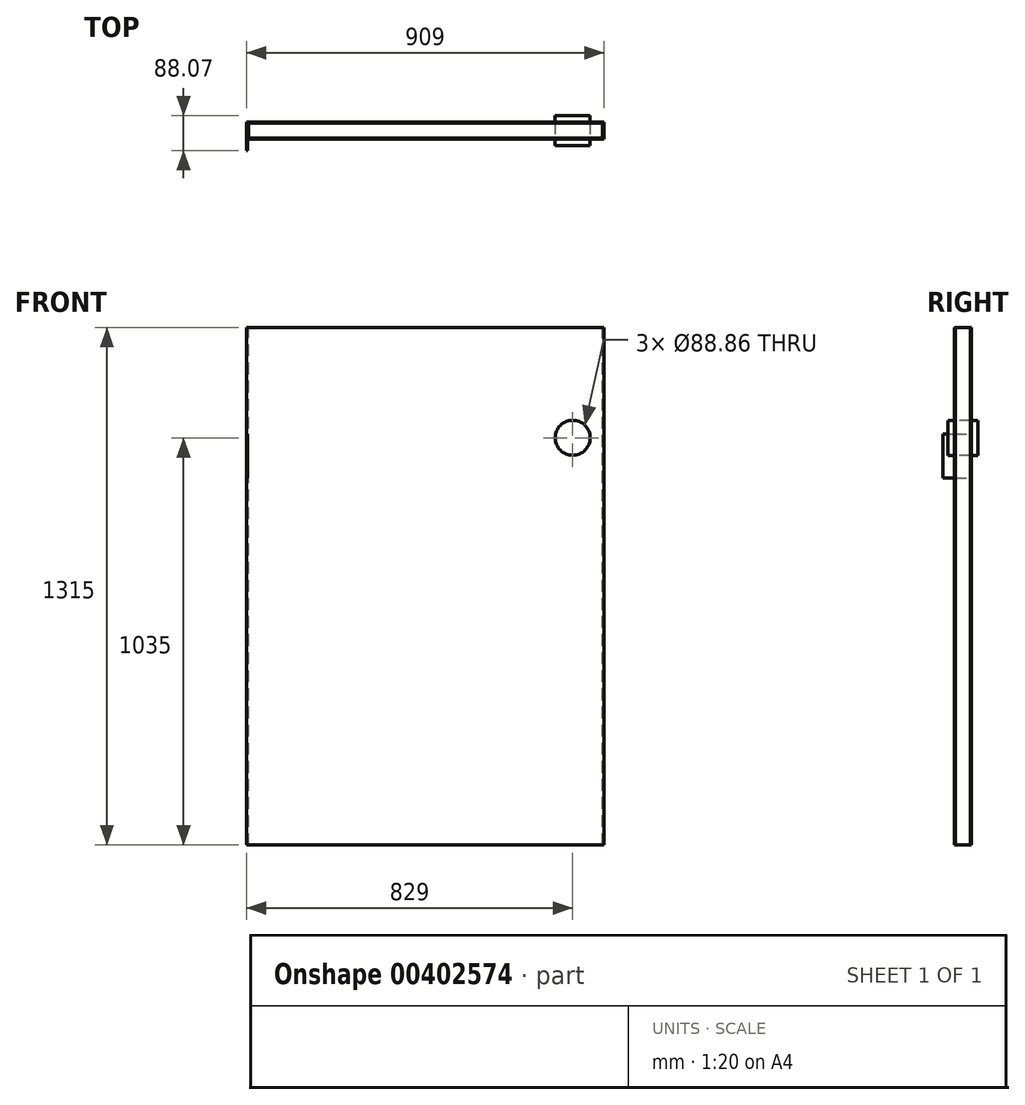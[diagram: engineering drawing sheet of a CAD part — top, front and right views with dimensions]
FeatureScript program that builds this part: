
annotation { "Feature Type Name" : "Feature", "Feature Type Description" : "" }
export const myFeature = defineFeature(function(context is Context, id is Id, definition is map)
    precondition{}
    {
        {
            var Q0;
            Q0=qCreatedBy(makeId("Front.planeOp"),FACE);
            var sketch = newSketch(context, id + "F0", { "sketchPlane" : qUnion([Q0])});
            skLineSegment(sketch, "E0.bottom", {"start": v(-454.5, 657.5) * mm, "end": v(454.5, 657.5) * mm});
            skLineSegment(sketch, "E0.top", {"start": v(-454.5, -657.5) * mm, "end": v(454.5, -657.5) * mm});
            skLineSegment(sketch, "E0.left", {"start": v(-454.5, 657.5) * mm, "end": v(-454.5, -657.5) * mm});
            skLineSegment(sketch, "E0.right", {"start": v(454.5, 657.5) * mm, "end": v(454.5, -657.5) * mm});
            skPoint(sketch, "E0.middle", {"position": v(0, 0) * mm});
            skSolve(sketch);
        }
        {
            var Q0;
            Q0=makeQuery(id+"F0.imprint","IMPRINT",FACE,{"disambiguationData":[TD([[makeQuery(id+"F0.imprint","IMPRINT",EDGE,{"derivedFrom":sQuery(id+"F0.wireOp",EDGE,"E0.bottom")}),-1.0]])]});
            extrude(context, id + "F1", {"entities" : qUnion([Q0]), "depth" : 43.25 * mm});
        }
        {
            var Q0;
            Q0=makeQuery(id+"F1.opExtrude","CAP_FACE",FACE,{"disambiguationData":[OSD([sQuery(id+"F0.wireOp",EDGE,"E0.bottom"),sQuery(id+"F0.wireOp",EDGE,"E0.top"),sQuery(id+"F0.wireOp",EDGE,"E0.left"),sQuery(id+"F0.wireOp",EDGE,"E0.right")])],"isStart":false});
            extrude(context, id + "F2", {"entities" : qUnion([Q0]), "oppositeDirection" : true, "depth" : 2.81 * mm});
        }
        {
            var Q0;
            Q0=makeQuery(id+"F1.opExtrude","CAP_FACE",FACE,{"disambiguationData":[OSD([sQuery(id+"F0.wireOp",EDGE,"E0.bottom"),sQuery(id+"F0.wireOp",EDGE,"E0.top"),sQuery(id+"F0.wireOp",EDGE,"E0.left"),sQuery(id+"F0.wireOp",EDGE,"E0.right")])],"isStart":true});
            extrude(context, id + "F3", {"entities" : qUnion([Q0]), "oppositeDirection" : true, "depth" : 2.81 * mm});
        }
        {
            var Q0;
            Q0=makeQuery(id+"F1.opExtrude","CAP_FACE",FACE,{"disambiguationData":[OSD([sQuery(id+"F0.wireOp",EDGE,"E0.bottom"),sQuery(id+"F0.wireOp",EDGE,"E0.top"),sQuery(id+"F0.wireOp",EDGE,"E0.left"),sQuery(id+"F0.wireOp",EDGE,"E0.right")])],"isStart":false});
            var sketch = newSketch(context, id + "F4", { "sketchPlane" : qUnion([Q0])});
            skLineSegment(sketch, "E1", {"start": v(407.48, 657.5) * mm, "end": v(407.48, 377.5) * mm});
            skLineSegment(sketch, "E2", {"start": v(454.5, 377.5) * mm, "end": v(374.5, 377.5) * mm});
            skPoint(sketch, "E3", {"position": v(374.5, 377.5) * mm});
            skCircle(sketch, "E4", {"center": v(374.5, 377.5) * mm, "radius": 44.43 * mm});
            skSolve(sketch);
        }
        {
            var Q0;
            {var subQ0=sQuery(id+"F4.wireOp",EDGE,"E2");var subQ1=sQuery(id+"F4.wireOp",EDGE,"E1");var subQ2=makeQuery(id+"F4.imprint","INTERSECT",VERTEX,{"derivedFrom":[subQ1,subQ0]});Q0=makeQuery(id+"F4.imprint","IMPRINT",FACE,{"disambiguationData":[TD([[makeQuery(id+"F4.imprint","IMPRINT",EDGE,{"disambiguationData":[TD([[subQ2,1.0]])],"derivedFrom":subQ1}),1.0]])]});}
            var Q1;
            {var subQ0=sQuery(id+"F4.wireOp",EDGE,"E2");var subQ1=sQuery(id+"F4.wireOp",EDGE,"E1");var subQ2=makeQuery(id+"F4.imprint","INTERSECT",VERTEX,{"derivedFrom":[subQ1,subQ0]});Q1=makeQuery(id+"F4.imprint","IMPRINT",FACE,{"disambiguationData":[TD([[makeQuery(id+"F4.imprint","IMPRINT",EDGE,{"disambiguationData":[TD([[subQ2,1.0]])],"derivedFrom":subQ1}),-1.0]])]});}
            extrude(context, id + "F5", {"entities" : qUnion([Q0, Q1]), "operationType" : NewBodyOperationType.REMOVE, "endBound" : BoundingType.THROUGH_ALL, "oppositeDirection" : true, "depth" : 15.73 * mm});
        }
        {
            var Q0;
            Q0=makeQuery(id+"F1.opExtrude","CAP_FACE",FACE,{"disambiguationData":[OSD([sQuery(id+"F0.wireOp",EDGE,"E0.bottom"),sQuery(id+"F0.wireOp",EDGE,"E0.top"),sQuery(id+"F0.wireOp",EDGE,"E0.left"),sQuery(id+"F0.wireOp",EDGE,"E0.right")])],"isStart":true});
            var sketch = newSketch(context, id + "F6", { "sketchPlane" : qUnion([Q0])});
            skPoint(sketch, "E5", {"position": v(451.14, 387.5) * mm});
            skLineSegment(sketch, "E6.bottom", {"start": v(451.14, 387.5) * mm, "end": v(454.5, 387.5) * mm});
            skLineSegment(sketch, "E6.top", {"start": v(451.14, 274.8) * mm, "end": v(454.5, 274.8) * mm});
            skLineSegment(sketch, "E6.left", {"start": v(451.14, 387.5) * mm, "end": v(451.14, 274.8) * mm});
            skLineSegment(sketch, "E6.right", {"start": v(454.5, 387.5) * mm, "end": v(454.5, 274.8) * mm});
            skSolve(sketch);
        }
        {
            var Q0;
            Q0=makeQuery(id+"F6.imprint","IMPRINT",FACE,{"disambiguationData":[TD([[makeQuery(id+"F6.imprint","IMPRINT",EDGE,{"derivedFrom":sQuery(id+"F6.wireOp",EDGE,"E6.bottom")}),-1.0]])]});
            extrude(context, id + "F7", {"entities" : qUnion([Q0]), "operationType" : NewBodyOperationType.REMOVE, "endBound" : BoundingType.THROUGH_ALL, "oppositeDirection" : true, "depth" : 28 * mm});
        }
        {
            var Q0;
            Q0=makeQuery(id+"F1.opExtrude","CAP_FACE",FACE,{"disambiguationData":[OSD([sQuery(id+"F0.wireOp",EDGE,"E0.bottom"),sQuery(id+"F0.wireOp",EDGE,"E0.top"),sQuery(id+"F0.wireOp",EDGE,"E0.left"),sQuery(id+"F0.wireOp",EDGE,"E0.right")])],"isStart":false});
            var sketch = newSketch(context, id + "F8", { "sketchPlane" : qUnion([Q0])});
            skCircle(sketch, "E7.0", {"center": v(374.5, 377.5) * mm, "radius": 44.43 * mm});
            skSolve(sketch);
        }
        {
            var Q0;
            Q0=qSketchRegion(id+"F8",true);
            extrude(context, id + "F9", {"entities" : qUnion([Q0]), "depth" : 16 * mm});
        }
        {
            var Q0;
            Q0=makeQuery(id+"F3.opExtrude","CAP_FACE",FACE,{"disambiguationData":[OSD([sQuery(id+"F0.wireOp",EDGE,"E0.bottom"),sQuery(id+"F0.wireOp",EDGE,"E0.top"),sQuery(id+"F0.wireOp",EDGE,"E0.left"),sQuery(id+"F0.wireOp",EDGE,"E0.right")])],"isStart":true});
            var sketch = newSketch(context, id + "F10", { "sketchPlane" : qUnion([Q0])});
            skCircle(sketch, "E8.0", {"center": v(-374.5, 377.5) * mm, "radius": 44.43 * mm});
            skSolve(sketch);
        }
        {
            var Q0;
            Q0=qSketchRegion(id+"F10",true);
            extrude(context, id + "F11", {"entities" : qUnion([Q0]), "depth" : 16 * mm});
        }
        {
            var Q0;
            Q0=makeQuery(id+"F1.opExtrude","CAP_FACE",FACE,{"disambiguationData":[OSD([sQuery(id+"F0.wireOp",EDGE,"E0.bottom"),sQuery(id+"F0.wireOp",EDGE,"E0.top"),sQuery(id+"F0.wireOp",EDGE,"E0.left"),sQuery(id+"F0.wireOp",EDGE,"E0.right")])],"isStart":false});
            var sketch = newSketch(context, id + "F12", { "sketchPlane" : qUnion([Q0])});
            skLineSegment(sketch, "E9", {"start": v(-454.5, 387.5) * mm, "end": v(-454.5, 274.8) * mm});
            skLineSegment(sketch, "E10", {"start": v(-454.5, 274.8) * mm, "end": v(-451.14, 274.8) * mm});
            skLineSegment(sketch, "E11", {"start": v(-451.14, 274.8) * mm, "end": v(-451.14, 387.5) * mm});
            skLineSegment(sketch, "E12", {"start": v(-451.14, 387.5) * mm, "end": v(-454.5, 387.5) * mm});
            skSolve(sketch);
        }
        {
            var Q0;
            Q0=makeQuery(id+"F12.imprint","IMPRINT",FACE,{"disambiguationData":[TD([[makeQuery(id+"F12.imprint","IMPRINT",EDGE,{"derivedFrom":sQuery(id+"F12.wireOp",EDGE,"E9")}),1.0]])]});
            extrude(context, id + "F13", {"entities" : qUnion([Q0]), "depth" : 28.82 * mm});
        }
        {
            var Q0;
            Q0=makeQuery(id+"F1.opExtrude","SWEPT_FACE",FACE,{"disambiguationData":[OSD([sQuery(id+"F0.wireOp",EDGE,"E0.bottom")])]});
            var sketch = newSketch(context, id + "F14", { "sketchPlane" : qUnion([Q0])});
            skLineSegment(sketch, "E13.1", {"start": v(-454.5, -2.81) * mm, "end": v(-449.5, -2.81) * mm});
            skLineSegment(sketch, "E14", {"start": v(-454.5, -40.44) * mm, "end": v(-454.5, -2.81) * mm});
            skLineSegment(sketch, "E15", {"start": v(-454.5, -40.44) * mm, "end": v(-449.5, -40.44) * mm});
            skLineSegment(sketch, "E16", {"start": v(-449.5, -40.44) * mm, "end": v(-449.5, -40.44) * mm});
            skLineSegment(sketch, "E17", {"start": v(-449.5, -40.44) * mm, "end": v(-449.5, -2.81) * mm});
            skLineSegment(sketch, "E18.0", {"start": v(-454.5, -2.81) * mm, "end": v(454.5, -2.81) * mm});
            skLineSegment(sketch, "E18.1", {"start": v(-454.5, -40.44) * mm, "end": v(454.5, -40.44) * mm});
            skLineSegment(sketch, "E19", {"start": v(454.5, -40.44) * mm, "end": v(454.5, -2.81) * mm});
            skLineSegment(sketch, "E20", {"start": v(454.5, -40.44) * mm, "end": v(449.5, -40.44) * mm});
            skLineSegment(sketch, "E21", {"start": v(449.5, -40.44) * mm, "end": v(449.5, -2.81) * mm});
            skLineSegment(sketch, "E22", {"start": v(449.5, -2.81) * mm, "end": v(454.5, -2.81) * mm});
            skSolve(sketch);
        }
        {
            var Q0;
            {var subQ0=sQuery(id+"F14.wireOp",EDGE,"E14");Q0=makeQuery(id+"F14.imprint","IMPRINT",FACE,{"disambiguationData":[TD([[makeQuery(id+"F14.imprint","IMPRINT",EDGE,{"derivedFrom":subQ0}),-1.0]])]});}
            var Q1;
            Q1=makeQuery(id+"F14.imprint","IMPRINT",FACE,{"disambiguationData":[TD([[makeQuery(id+"F14.imprint","IMPRINT",EDGE,{"derivedFrom":sQuery(id+"F14.wireOp",EDGE,"E19")}),1.0]])]});
            extrude(context, id + "F15", {"entities" : qUnion([Q0, Q1]), "oppositeDirection" : true, "depth" : 1315 * mm});
        }
    });
